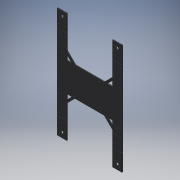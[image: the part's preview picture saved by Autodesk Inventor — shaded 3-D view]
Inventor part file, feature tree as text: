
AUTODESK INVENTOR PART (.ipt)
format: ipt  version: 2018 (Build 220112000, 112)  size: 278,016 bytes
history: native  units: mm
features: other x5, plane x2, mirror x2, sketch x1, extrude x1, reference x1
ambient origin geometry x8: Origin, YZ Plane, XZ Plane, XY Plane, X Axis, Y Axis, Z Axis, Center Point
bodies: Volumenkörper1 (feature_tree)
feature tree (12):
  sketch  "Skizze1"  dims[d10=100.0mm d12=30.0mm d13=170.0mm d14=45.0mm d15=3.0mm d16=0.0mm d17=0.0mm d18=0.0mm d22=5.0mm d23=4.0mm d26=3.4mm d59=30.0mm d60=8.0mm d61=15.0mm d64=3.4mm d65=3.4mm d66=3.4mm d67=3.4mm d70=7.802084mm d74=16.0mm d75=19.0mm d76=90.0deg d78=0.5mm d79=52.0mm d82=3.4mm d83=3.4mm d84=7.0mm d85=7.0mm d88=15.0mm d89=10.0mm d90=3.4mm d94=3.4mm d95=15.0mm]
  extrude  "Extrusion1"  Depth=30.0mm
  plane  "Arbeitsebene1"
  plane  "Arbeitsebene2"
  mirror  "Spiegeln1"
  other  "Arbeitsachse1"
  mirror  "Spiegeln2"
  reference  "Referenz1"
  other  "<userpath>\OneDrive\Development\Mohne\03_Konstruktion\Mohne komplett.iam"
  other  "Mohne komplett.iam"
  other  "EMax Motor:1"
  other  "01000A-040-002-LE_6"
